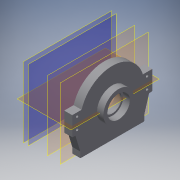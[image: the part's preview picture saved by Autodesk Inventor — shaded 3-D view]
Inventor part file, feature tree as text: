
AUTODESK INVENTOR PART (.ipt)
format: ipt  version: 2019 (Build 230136000, 136)  size: 510,464 bytes
history: native  units: mm
features: sketch x26, extrude x21, mirror x13, plane x12, projected_geometry x11, fillet x4, hole x3, other x2
ambient origin geometry x8: Origin, YZ Plane, XZ Plane, XY Plane, X Axis, Y Axis, Z Axis, Center Point
bodies: Body1 (feature_tree)
feature tree (92):
  other  "實體1"
  extrude  "擠出1"  Depth=123.43mm
  plane  "工作平面2"
  extrude  "擠出3"  Depth=160.0mm
  plane  "工作平面3"
  extrude  "擠出4"  Depth=120.0mm TaperAngle=0.0deg
  extrude  "擠出5"  [1 undecoded]
  plane  "工作平面4"
  extrude  "擠出7"  Depth=130.0mm
  plane  "工作平面5"
  extrude  "擠出9"  Depth=15.0mm TaperAngle=0.0deg
  extrude  "擠出10"  [1 undecoded]
  extrude  "擠出11"  Depth=140.0mm
  extrude  "擠出12"  Depth=10.0mm TaperAngle=0.0deg
  mirror  "鏡射1"
  fillet  "圓角2"  Radius=10.0mm
  fillet  "圓角3"  Radius=10.0mm
  sketch  "草圖16"
  plane  "工作平面7"
  mirror  "鏡射2"
  fillet  "圓角5"  [1 undecoded]
  fillet  "圓角6"  Radius=10.0mm
  plane  "工作平面8"
  plane  "工作平面9"
  sketch  "草圖20"
  extrude  "擠出15"  [1 undecoded]
  plane  "工作平面10"
  extrude  "擠出16"  Depth=10.0mm
  extrude  "擠出17"  Depth=10.0mm TaperAngle=0.0deg
  plane  "工作平面11"
  extrude  "擠出19"  Depth=10.0mm TaperAngle=0.0deg
  extrude  "擠出20"  Depth=160.0mm
  mirror  "鏡射3"
  mirror  "鏡射4"
  extrude  "擠出21"  Depth=80.0mm
  mirror  "鏡射7"
  plane  "工作平面15"
  mirror  "鏡射9"
  hole  "孔2"  [1 undecoded]
  mirror  "鏡射10"
  mirror  "鏡射11"
  hole  "孔3"  [1 undecoded]
  mirror  "鏡射12"
  mirror  "鏡射13"
  extrude  "擠出22"  Depth=160.0mm
  extrude  "擠出23"  Depth=120.0mm TaperAngle=0.0deg
  extrude  "擠出24"  Depth=120.0mm TaperAngle=0.0deg
  extrude  "擠出25"  Depth=25.0mm
  extrude  "擠出27"  Depth=20.0mm
  extrude  "擠出28"  Depth=2.0mm
  mirror  "鏡射14"
  plane  "工作平面17"
  hole  "孔4"  [1 undecoded]
  mirror  "鏡射15"
  mirror  "鏡射16"
  other  "分割1"
  sketch  "草圖1"
  sketch  "草圖4"
  sketch  "草圖6"
  sketch  "草圖7"
  projected_geometry  "投影迴路1"
  sketch  "草圖9"
  projected_geometry  "投影迴路4"
  sketch  "草圖11"
  sketch  "草圖12"
  projected_geometry  "投影迴路6"
  sketch  "草圖13"
  projected_geometry  "投影迴路7"
  sketch  "草圖14"
  plane  "工作平面6"
  sketch  "草圖17"
  projected_geometry  "投影迴路8"
  sketch  "草圖24"
  projected_geometry  "投影迴路11"
  sketch  "草圖25"
  sketch  "草圖26"
  sketch  "草圖27"
  sketch  "草圖28"
  sketch  "草圖29"
  projected_geometry  "投影迴路12"
  sketch  "草圖30"
  sketch  "草圖31"
  sketch  "草圖32"
  projected_geometry  "投影迴路13"
  projected_geometry  "投影迴路14"
  projected_geometry  "投影迴路15"
  sketch  "草圖33"
  sketch  "草圖34"
  sketch  "草圖35"
  projected_geometry  "投影迴路16"
  sketch  "草圖36"
  sketch  "草圖37"
note: 7 required parameter values undecoded (feature->parameter linkage not recoverable at this tier; creation-order binding heuristic only, values carry confidence <= 0.55)
